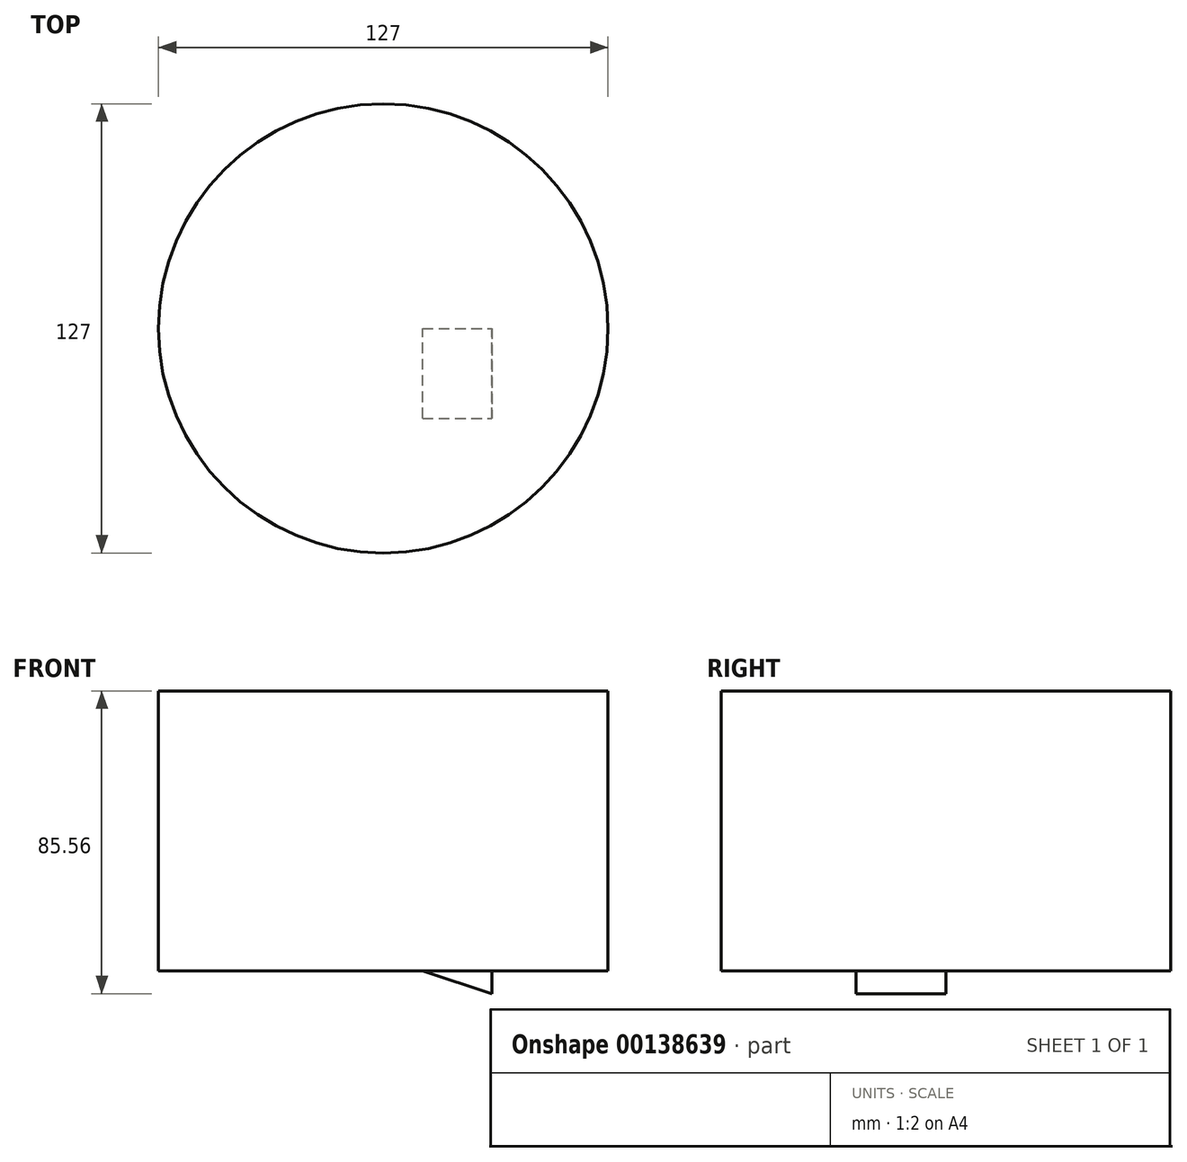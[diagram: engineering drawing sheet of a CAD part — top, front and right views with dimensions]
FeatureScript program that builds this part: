
annotation { "Feature Type Name" : "Feature", "Feature Type Description" : "" }
export const myFeature = defineFeature(function(context is Context, id is Id, definition is map)
    precondition{}
    {
        {
            var Q0;
            Q0=qCreatedBy(makeId("Top.planeOp"),FACE);
            var sketch = newSketch(context, id + "F0", { "sketchPlane" : qUnion([Q0])});
            skCircle(sketch, "E0", {"center": v(0, 0) * mm, "radius": 63.5 * mm});
            skSolve(sketch);
        }
        {
            var Q0;
            Q0=makeQuery(id+"F0.imprint","IMPRINT",FACE,{"disambiguationData":[TD([[makeQuery(id+"F0.imprint","IMPRINT",EDGE,{"derivedFrom":sQuery(id+"F0.wireOp",EDGE,"E0")}),1.0]])]});
            var Q1;
            Q1=sQuery(id+"F0.wireOp",EDGE,"E0");
            extrude(context, id + "F1", {"entities" : qUnion([Q0]), "surfaceEntities" : qUnion([Q1]), "depth" : 79.14 * mm});
        }
        {
            var Q0;
            Q0=qCreatedBy(makeId("Front.planeOp"),FACE);
            var sketch = newSketch(context, id + "F2", { "sketchPlane" : qUnion([Q0])});
            skLineSegment(sketch, "E1", {"start": v(0, 48.59) * mm, "end": v(11.1, 0) * mm});
            skLineSegment(sketch, "E2", {"start": v(11.1, 0) * mm, "end": v(30.68, -6.42) * mm});
            skLineSegment(sketch, "E3", {"start": v(30.68, -6.42) * mm, "end": v(31.4, 51.82) * mm});
            skLineSegment(sketch, "E4", {"start": v(31.4, 51.82) * mm, "end": v(0, 48.59) * mm});
            skSolve(sketch);
        }
        {
            var Q0;
            Q0=makeQuery(id+"F2.imprint","IMPRINT",FACE,{"disambiguationData":[TD([[makeQuery(id+"F2.imprint","IMPRINT",EDGE,{"derivedFrom":sQuery(id+"F2.wireOp",EDGE,"E1")}),1.0]])]});
            extrude(context, id + "F3", {"entities" : qUnion([Q0]), "operationType" : NewBodyOperationType.ADD, "depth" : 25.4 * mm});
        }
    });
